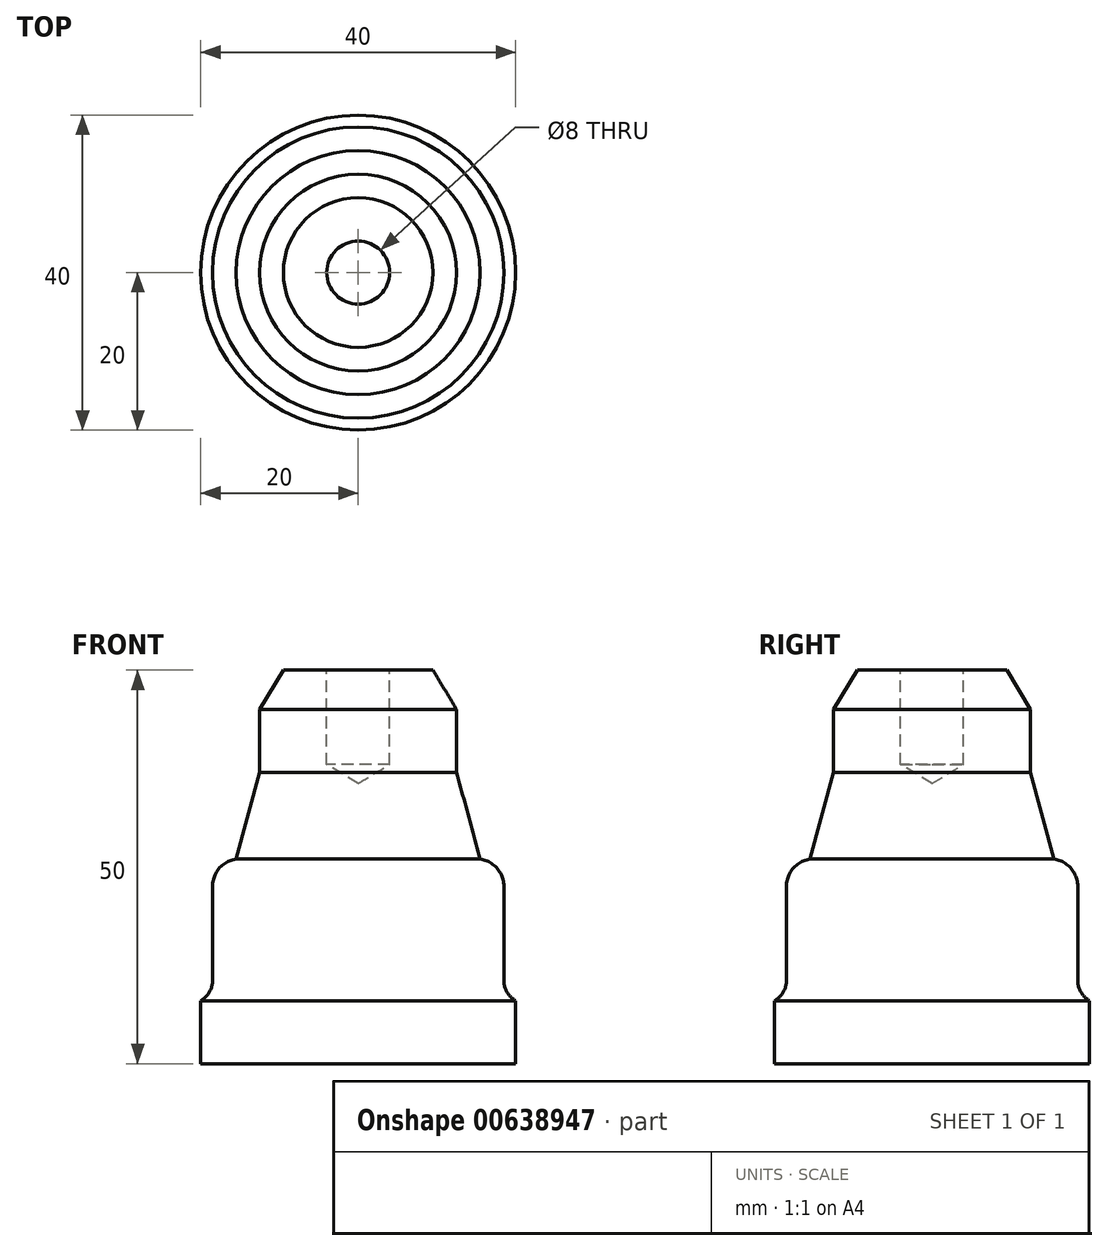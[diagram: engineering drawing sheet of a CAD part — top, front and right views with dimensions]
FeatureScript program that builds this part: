
annotation { "Feature Type Name" : "Feature", "Feature Type Description" : "" }
export const myFeature = defineFeature(function(context is Context, id is Id, definition is map)
    precondition{}
    {
        {
            var Q0;
            Q0=qCreatedBy(makeId("Front.planeOp"),FACE);
            var sketch = newSketch(context, id + "F0", { "sketchPlane" : qUnion([Q0])});
            skLineSegment(sketch, "E0", {"start": v(0, -50) * mm, "end": v(20, -50) * mm});
            skLineSegment(sketch, "E1", {"start": v(20, -50) * mm, "end": v(20, -42) * mm});
            skLineSegment(sketch, "E2", {"start": v(18.5, -39.4) * mm, "end": v(18.5, -27.46) * mm});
            skLineSegment(sketch, "E3", {"start": v(15.5, -24) * mm, "end": v(12.5, -13) * mm});
            skLineSegment(sketch, "E4", {"start": v(12.5, -13) * mm, "end": v(12.5, -5) * mm});
            skLineSegment(sketch, "E5", {"start": v(12.5, -5) * mm, "end": v(9.5, 0) * mm});
            skLineSegment(sketch, "E6", {"start": v(9.5, 0) * mm, "end": v(0, 0) * mm});
            skLineSegment(sketch, "E7", {"start": v(0, 0) * mm, "end": v(0, -50) * mm});
            skArc(sketch, "E8", {"start": v(18.5, -39.4) * mm, "mid": v(18.9, -40.9) * mm, "end": v(20, -42) * mm});
            skArc(sketch, "E9", {"start": v(18.5, -27.46) * mm, "mid": v(17.65, -25.17) * mm, "end": v(15.5, -24) * mm});
            skSolve(sketch);
        }
        {
            var Q0;
            Q0=makeQuery(id+"F0.imprint","IMPRINT",FACE,{"disambiguationData":[TD([[makeQuery(id+"F0.imprint","IMPRINT",EDGE,{"derivedFrom":sQuery(id+"F0.wireOp",EDGE,"E0")}),1.0]])]});
            var Q1;
            Q1=sQuery(id+"F0.wireOp",EDGE,"E7");
            revolve(context, id + "F1", {"entities" : qUnion([Q0]), "axis" : qUnion([Q1]), "revolveType" : RevolveType.FULL});
        }
        {
            var Q0;
            Q0=makeQuery(id+"F1.opRevolve","SWEPT_FACE",FACE,{"disambiguationData":[OSD([sQuery(id+"F0.wireOp",EDGE,"E6")])]});
            var sketch = newSketch(context, id + "F2", { "sketchPlane" : qUnion([Q0])});
            skPoint(sketch, "E10", {"position": v(0, 0) * mm});
            skSolve(sketch);
        }
        {
            var Q0;
            Q0=sQuery(id+"F2.wireOp",VERTEX,"E10");
            var Q1;
            Q1=makeQuery(id+"F1.opRevolve","SWEPT_BODY",BODY,{"disambiguationData":[OSD([sQuery(id+"F0.wireOp",EDGE,"E0"),sQuery(id+"F0.wireOp",EDGE,"E1"),sQuery(id+"F0.wireOp",EDGE,"E2"),sQuery(id+"F0.wireOp",EDGE,"E3"),sQuery(id+"F0.wireOp",EDGE,"E4"),sQuery(id+"F0.wireOp",EDGE,"E5"),sQuery(id+"F0.wireOp",EDGE,"E6"),sQuery(id+"F0.wireOp",EDGE,"E7"),sQuery(id+"F0.wireOp",EDGE,"E8"),sQuery(id+"F0.wireOp",EDGE,"E9")])]});
            hole(context, id + "F3", {"style" : HoleStyle.SIMPLE, "endStyle" : HoleEndStyle.BLIND, "holeDiameter" : 8 * mm, "majorDiameter" : 5 * mm, "holeDepth" : 12 * mm, "isTappedThrough" : true, "tappedDepth" : 12 * mm, "tapClearance" : 3, "locations" : qUnion([Q0]), "scope" : qUnion([Q1])});
        }
    });
